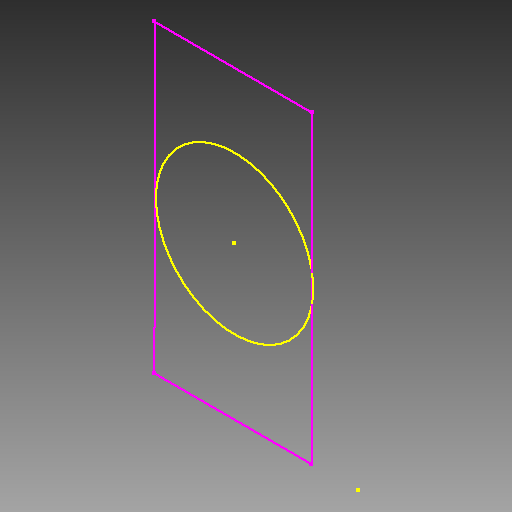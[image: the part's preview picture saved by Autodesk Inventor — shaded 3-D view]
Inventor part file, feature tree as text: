
AUTODESK INVENTOR PART (.ipt)
format: ipt  version: 2018 (Build 220112000, 112)  size: 71,680 bytes
history: native  units: mm
features: other x1, sketch x1
ambient origin geometry x8: Origin, YZ Plane, XZ Plane, XY Plane, X Axis, Y Axis, Z Axis, Center Point
feature tree (2):
  other  "Working Axis etc.ipt"
  sketch  "Sketch1"  dims[d0=10.0mm]
